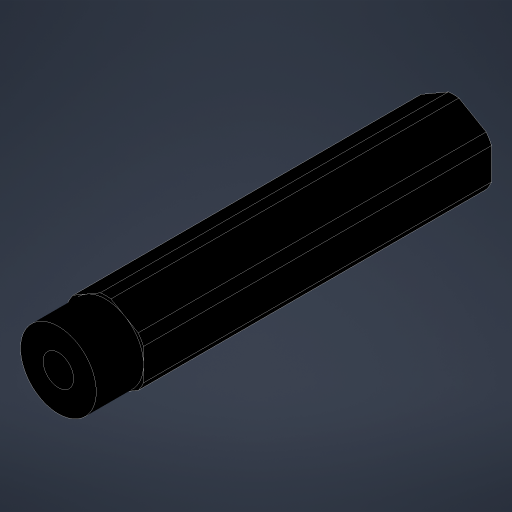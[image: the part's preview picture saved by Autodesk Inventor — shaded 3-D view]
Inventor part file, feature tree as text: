
AUTODESK INVENTOR PART (.ipt)
format: ipt  version: 2023.4 (Build 274418000, 418)  size: 216,064 bytes
history: native  units: in
note: dims shown in document units (in); Inventor stores cm internally (conversion verified against a paired STEP export)
features: extrude x3, projected_geometry x3, hole x1, sketch x1
ambient origin geometry x8: Origin, YZ Plane, XZ Plane, XY Plane, X Axis, Y Axis, Z Axis, Center Point
bodies: Solid1 (feature_tree)
feature tree (8):
  extrude  "Extrusion1"  Depth=0.5in
  hole  "Hole1"  [1 undecoded]
  extrude  "Extrusion3"  Depth=0.312in TaperAngle=0.0deg
  extrude  "Extrusion4"  Depth=0.5in
  sketch  "Sketch5"  dims[d2=0.0in d9=0.625in d10=0.385in d11=0.25in d12=0.5635in d13=1.0in d14=0.8108in d16=0.7in d17=0.0in d18=0.0in d19=0.312in d20=0.0in d21=0.5in]
  projected_geometry  "Projected Loop2"
  projected_geometry  "Project Cut Edges1"
  projected_geometry  "Project Cut Edges2"
note: 1 required parameter value undecoded (feature->parameter linkage not recoverable at this tier; creation-order binding heuristic only, values carry confidence <= 0.55)
